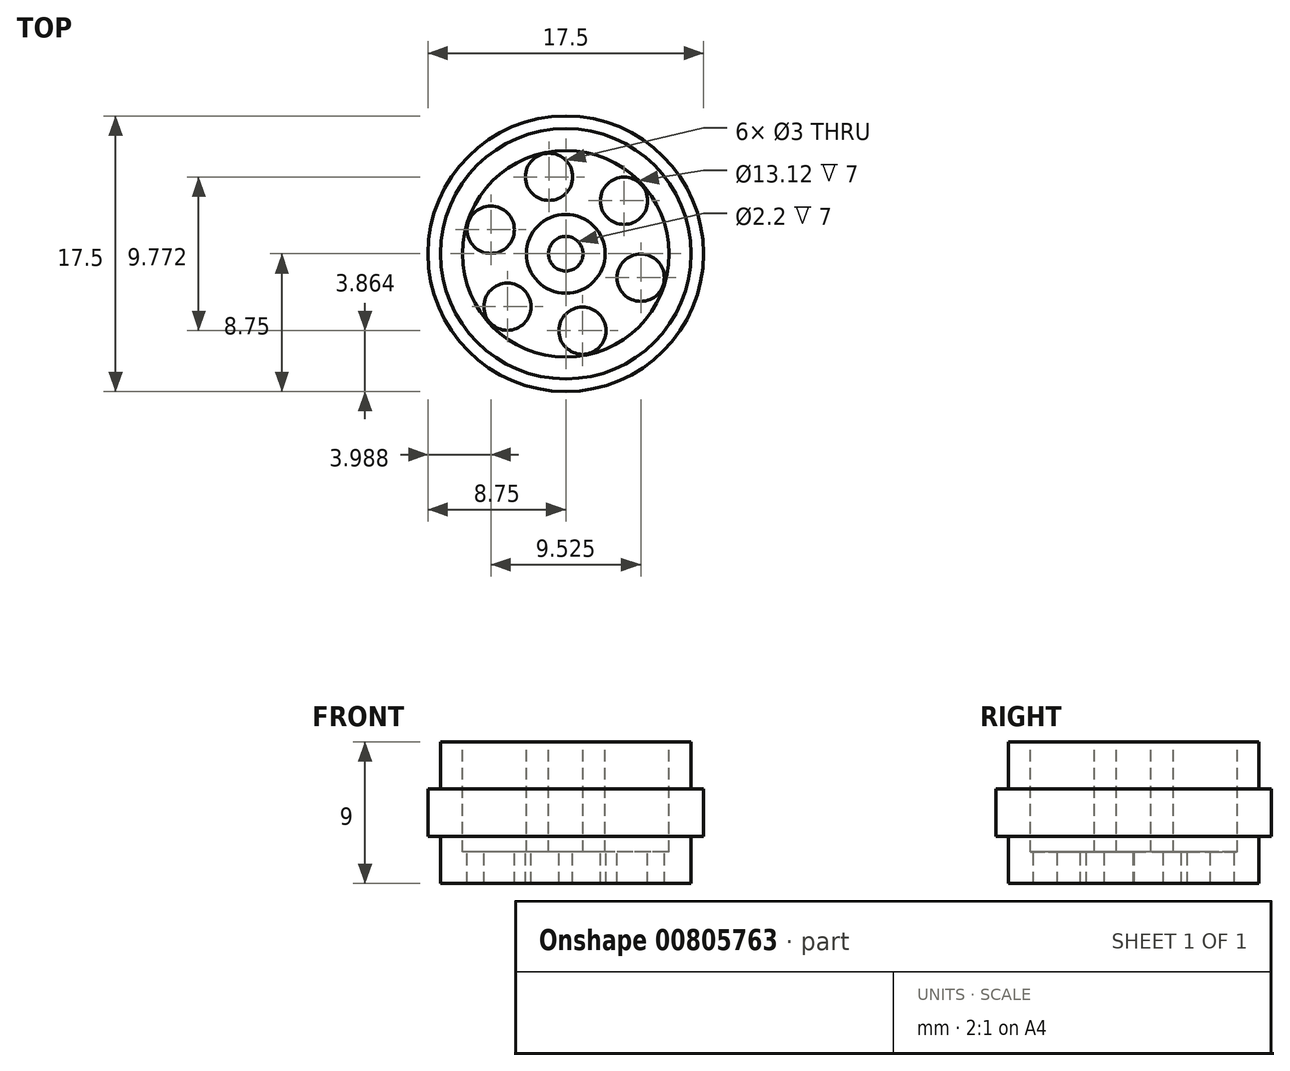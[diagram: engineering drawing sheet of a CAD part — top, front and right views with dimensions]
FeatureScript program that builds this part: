
annotation { "Feature Type Name" : "Feature", "Feature Type Description" : "" }
export const myFeature = defineFeature(function(context is Context, id is Id, definition is map)
    precondition{}
    {
        {
            var Q0;
            Q0=qCreatedBy(makeId("Top.planeOp"),FACE);
            var sketch = newSketch(context, id + "F0", { "sketchPlane" : qUnion([Q0])});
            skCircle(sketch, "E0", {"center": v(0, 0) * mm, "radius": 7.95 * mm});
            skSolve(sketch);
        }
        {
            var Q0;
            Q0=qSketchRegion(id+"F0",true);
            extrude(context, id + "F1", {"entities" : qUnion([Q0]), "depth" : 3 * mm});
        }
        {
            var Q0;
            Q0=makeQuery(id+"F1.opExtrude","CAP_FACE",FACE,{"disambiguationData":[OSD([sQuery(id+"F0.wireOp",EDGE,"E0")])],"isStart":false});
            var sketch = newSketch(context, id + "F2", { "sketchPlane" : qUnion([Q0])});
            skCircle(sketch, "E1", {"center": v(0, 0) * mm, "radius": 8.75 * mm});
            skSolve(sketch);
        }
        {
            var Q0;
            Q0=qSketchRegion(id+"F2",true);
            extrude(context, id + "F3", {"entities" : qUnion([Q0]), "operationType" : NewBodyOperationType.ADD, "depth" : 3 * mm});
        }
        {
            var Q0;
            Q0=makeQuery(id+"F3.opExtrude","CAP_FACE",FACE,{"disambiguationData":[OSD([sQuery(id+"F2.wireOp",EDGE,"E1")])],"isStart":false});
            var sketch = newSketch(context, id + "F4", { "sketchPlane" : qUnion([Q0])});
            skCircle(sketch, "E2", {"center": v(0, 0) * mm, "radius": 7.95 * mm});
            skSolve(sketch);
        }
        {
            var Q0;
            Q0=qSketchRegion(id+"F4",true);
            extrude(context, id + "F5", {"entities" : qUnion([Q0]), "operationType" : NewBodyOperationType.ADD, "depth" : 3 * mm});
        }
        {
            var Q0;
            Q0=makeQuery(id+"F5.opExtrude","CAP_FACE",FACE,{"disambiguationData":[OSD([sQuery(id+"F4.wireOp",EDGE,"E2")])],"isStart":false});
            var sketch = newSketch(context, id + "F6", { "sketchPlane" : qUnion([Q0])});
            skCircle(sketch, "E3", {"center": v(0, 0) * mm, "radius": 5 * mm, "construction": true});
            skCircle(sketch, "E4", {"center": v(3.7, 3.36) * mm, "radius": 1.5 * mm});
            skCircle(sketch, "E5.1.0", {"center": v(-1.06, 4.89) * mm, "radius": 1.5 * mm});
            skCircle(sketch, "E5.2.0", {"center": v(-4.76, 1.52) * mm, "radius": 1.5 * mm});
            skCircle(sketch, "E5.3.0", {"center": v(-3.7, -3.36) * mm, "radius": 1.5 * mm});
            skCircle(sketch, "E5.4.0", {"center": v(1.06, -4.89) * mm, "radius": 1.5 * mm});
            skCircle(sketch, "E5.5.0", {"center": v(4.76, -1.52) * mm, "radius": 1.5 * mm});
            skSolve(sketch);
        }
        {
            var Q0;
            Q0=qSketchRegion(id+"F6",true);
            extrude(context, id + "F7", {"entities" : qUnion([Q0]), "operationType" : NewBodyOperationType.REMOVE, "oppositeDirection" : true, "depth" : 25 * mm});
        }
        {
            var Q0;
            Q0=makeQuery(id+"F5.opExtrude","CAP_FACE",FACE,{"disambiguationData":[OSD([sQuery(id+"F4.wireOp",EDGE,"E2")])],"isStart":false});
            var sketch = newSketch(context, id + "F8", { "sketchPlane" : qUnion([Q0])});
            skCircle(sketch, "E6", {"center": v(0, 0) * mm, "radius": 1.1 * mm});
            skCircle(sketch, "E7", {"center": v(0, 0) * mm, "radius": 2.5 * mm});
            skCircle(sketch, "E8", {"center": v(0, 0) * mm, "radius": 6.56 * mm});
            skSolve(sketch);
        }
        {
            var Q0;
            Q0=qSketchRegion(id+"F8",true);
            var Q1;
            Q1=makeQuery(id+"F8.imprint","IMPRINT",FACE,{"disambiguationData":[TD([[makeQuery(id+"F8.imprint","IMPRINT",EDGE,{"derivedFrom":sQuery(id+"F8.wireOp",EDGE,"E6")}),1.0]])]});
            extrude(context, id + "F9", {"entities" : qUnion([Q0, Q1]), "operationType" : NewBodyOperationType.REMOVE, "oppositeDirection" : true, "depth" : 7 * mm});
        }
    });
